# Revit family: F035-38x38x32
name_source: partatom
category: Furniture Systems
units: mm (PartAtom-declared; Revit-internal decimal feet)

## family parameters
Always vertical = Yes
Cut with Voids When Loaded = No
Part Type = Normal
Room Calculation Point = No
Round Connector Dimension = Use Diameter
Shared = No
Work Plane-Based = No

## types (2) — shared parameters
Back Fabric = <By Category>
Base = <By Category>
Description = Step Series - Three Step Inside Corner (1st step height 7", 2nd step height 23"))
Glide = <By Category>
LEG H = 0' - 1 1/2"
Low Profile = Black
Manufacturer = FOMCORE
Model = F035-38x38x32
Side Fabric = <By Category>
Step-1 Fabric = <By Category>
Step-2 Fabric = <By Category>
Step-3 Fabric = <By Category>
URL = https://fomcore.com

## per-type parameters (varying)
| type | G1 | L1 | LEG OPTIONS |
| F035-38x38x32-G1 | Yes | No | 1 |
| F035-38x38x32-L1 | No | Yes | 2 |

## geometry (parser evidence)
native form markers: Sweep x2
no freeform markers — native parametric forms only
